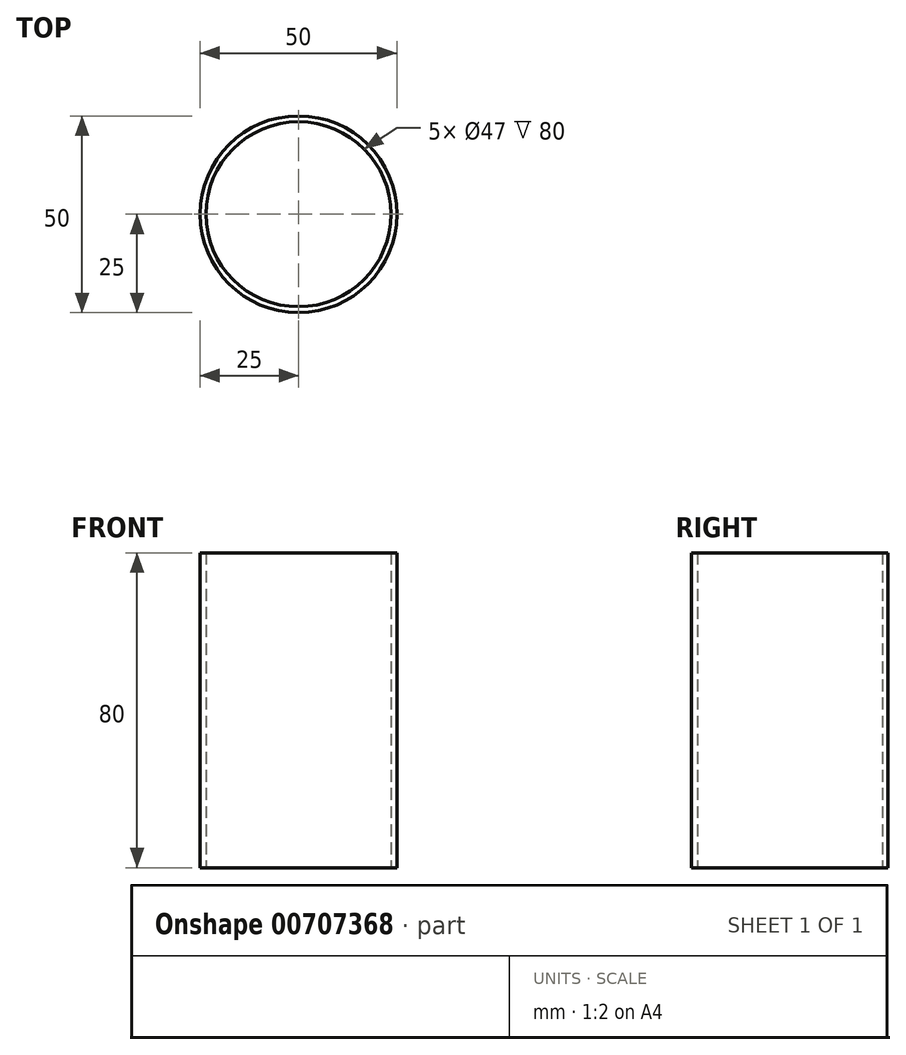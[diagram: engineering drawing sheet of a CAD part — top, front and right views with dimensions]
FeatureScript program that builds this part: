
annotation { "Feature Type Name" : "Feature", "Feature Type Description" : "" }
export const myFeature = defineFeature(function(context is Context, id is Id, definition is map)
    precondition{}
    {
        {
            var Q0;
            Q0=qCreatedBy(makeId("Top.planeOp"),FACE);
            var sketch = newSketch(context, id + "F0", { "sketchPlane" : qUnion([Q0])});
            skCircle(sketch, "E0", {"center": v(0, 0) * mm, "radius": 23.5 * mm});
            skCircle(sketch, "E1", {"center": v(0, 0) * mm, "radius": 25 * mm});
            skSolve(sketch);
        }
        {
            var Q0;
            Q0=makeQuery(id+"F0.imprint","IMPRINT",FACE,{"disambiguationData":[TD([[makeQuery(id+"F0.imprint","IMPRINT",EDGE,{"derivedFrom":sQuery(id+"F0.wireOp",EDGE,"E0")}),-1.0]])]});
            extrude(context, id + "F1", {"entities" : qUnion([Q0]), "depth" : 80 * mm, "offsetDistance" : 25 * mm});
        }
    });
